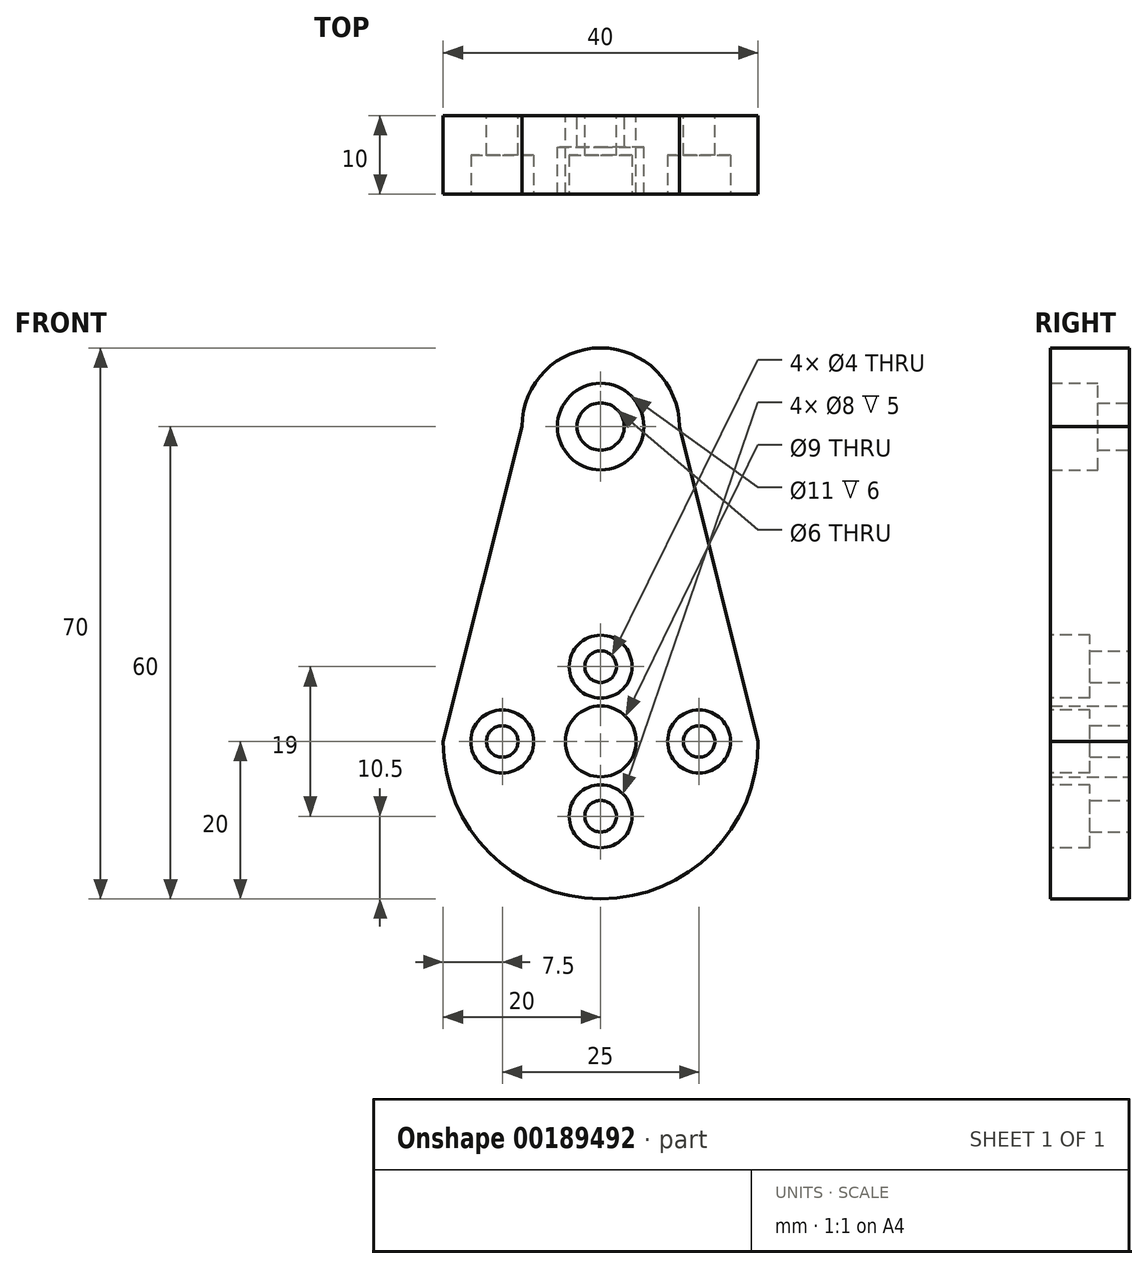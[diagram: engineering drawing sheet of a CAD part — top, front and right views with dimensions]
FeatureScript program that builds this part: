
annotation { "Feature Type Name" : "Feature", "Feature Type Description" : "" }
export const myFeature = defineFeature(function(context is Context, id is Id, definition is map)
    precondition{}
    {
        {
            var Q0;
            Q0=qCreatedBy(makeId("Front.planeOp"),FACE);
            var sketch = newSketch(context, id + "F0", { "sketchPlane" : qUnion([Q0])});
            skCircle(sketch, "E0", {"center": v(0, 0) * mm, "radius": 3 * mm});
            skCircle(sketch, "E1", {"center": v(0, 0) * mm, "radius": 5.5 * mm});
            skArc(sketch, "E2", {"start": v(10, 0) * mm, "mid": v(0, 10) * mm, "end": v(-10, 0) * mm});
            skArc(sketch, "E3", {"start": v(-20, -40) * mm, "mid": v(0, -60) * mm, "end": v(20, -40) * mm});
            skLineSegment(sketch, "E4", {"start": v(10, 0) * mm, "end": v(20, -40) * mm});
            skLineSegment(sketch, "E5", {"start": v(-10, 0) * mm, "end": v(-20, -40) * mm});
            skCircle(sketch, "E6", {"center": v(0, -40) * mm, "radius": 4.5 * mm});
            skCircle(sketch, "E7", {"center": v(-12.5, -40) * mm, "radius": 2 * mm});
            skCircle(sketch, "E8", {"center": v(12.5, -40) * mm, "radius": 2 * mm});
            skCircle(sketch, "E9", {"center": v(0, -30.5) * mm, "radius": 2 * mm});
            skCircle(sketch, "E10", {"center": v(0, -49.5) * mm, "radius": 2 * mm});
            skSolve(sketch);
        }
        {
            var Q0;
            Q0=makeQuery(id+"F0.imprint","IMPRINT",FACE,{"disambiguationData":[TD([[makeQuery(id+"F0.imprint","IMPRINT",EDGE,{"derivedFrom":sQuery(id+"F0.wireOp",EDGE,"E1")}),-1.0]])]});
            extrude(context, id + "F1", {"entities" : qUnion([Q0]), "depth" : 10 * mm});
        }
        {
            var Q0;
            Q0=makeQuery(id+"F0.imprint","IMPRINT",FACE,{"disambiguationData":[TD([[makeQuery(id+"F0.imprint","IMPRINT",EDGE,{"derivedFrom":sQuery(id+"F0.wireOp",EDGE,"E0")}),-1.0]])]});
            extrude(context, id + "F2", {"entities" : qUnion([Q0]), "operationType" : NewBodyOperationType.ADD, "depth" : 4 * mm});
        }
        {
            var Q0;
            Q0=makeQuery(id+"F1.opExtrude","CAP_FACE",FACE,{"disambiguationData":[OSD([sQuery(id+"F0.wireOp",EDGE,"E1"),sQuery(id+"F0.wireOp",EDGE,"E2"),sQuery(id+"F0.wireOp",EDGE,"E3"),sQuery(id+"F0.wireOp",EDGE,"E4"),sQuery(id+"F0.wireOp",EDGE,"E5"),sQuery(id+"F0.wireOp",EDGE,"E6"),sQuery(id+"F0.wireOp",EDGE,"E7"),sQuery(id+"F0.wireOp",EDGE,"E8"),sQuery(id+"F0.wireOp",EDGE,"E9"),sQuery(id+"F0.wireOp",EDGE,"E10")])],"isStart":false});
            var sketch = newSketch(context, id + "F3", { "sketchPlane" : qUnion([Q0])});
            skLineSegment(sketch, "E11.0.0", {"start": v(20, -40) * mm, "end": v(10, 0) * mm});
            skArc(sketch, "E11.0.1", {"start": v(10, 0) * mm, "mid": v(0, 10) * mm, "end": v(-10, 0) * mm});
            skLineSegment(sketch, "E11.0.2", {"start": v(-10, 0) * mm, "end": v(-20, -40) * mm});
            skArc(sketch, "E11.0.3", {"start": v(-20, -40) * mm, "mid": v(0, -60) * mm, "end": v(20, -40) * mm});
            skCircle(sketch, "E12.0", {"center": v(0, -30.5) * mm, "radius": 2 * mm});
            skCircle(sketch, "E13.0", {"center": v(-12.5, -40) * mm, "radius": 2 * mm});
            skCircle(sketch, "E14.0", {"center": v(0, -49.5) * mm, "radius": 2 * mm});
            skCircle(sketch, "E15.0", {"center": v(12.5, -40) * mm, "radius": 2 * mm});
            skCircle(sketch, "E16", {"center": v(0, -30.5) * mm, "radius": 4 * mm});
            skCircle(sketch, "E17", {"center": v(12.5, -40) * mm, "radius": 4 * mm});
            skCircle(sketch, "E18", {"center": v(0, -49.5) * mm, "radius": 4 * mm});
            skCircle(sketch, "E19", {"center": v(-12.5, -40) * mm, "radius": 4 * mm});
            skSolve(sketch);
        }
        {
            var Q0;
            Q0=makeQuery(id+"F3.imprint","IMPRINT",FACE,{"disambiguationData":[TD([[makeQuery(id+"F3.imprint","IMPRINT",EDGE,{"derivedFrom":sQuery(id+"F3.wireOp",EDGE,"E12.0")}),-1.0]])]});
            var Q1;
            Q1=makeQuery(id+"F3.imprint","IMPRINT",FACE,{"disambiguationData":[TD([[makeQuery(id+"F3.imprint","IMPRINT",EDGE,{"derivedFrom":sQuery(id+"F3.wireOp",EDGE,"E13.0")}),-1.0]])]});
            var Q2;
            Q2=makeQuery(id+"F3.imprint","IMPRINT",FACE,{"disambiguationData":[TD([[makeQuery(id+"F3.imprint","IMPRINT",EDGE,{"derivedFrom":sQuery(id+"F3.wireOp",EDGE,"E14.0")}),-1.0]])]});
            var Q3;
            Q3=makeQuery(id+"F3.imprint","IMPRINT",FACE,{"disambiguationData":[TD([[makeQuery(id+"F3.imprint","IMPRINT",EDGE,{"derivedFrom":sQuery(id+"F3.wireOp",EDGE,"E15.0")}),-1.0]])]});
            extrude(context, id + "F4", {"entities" : qUnion([Q0, Q1, Q2, Q3]), "operationType" : NewBodyOperationType.REMOVE, "oppositeDirection" : true, "depth" : 5 * mm});
        }
    });
